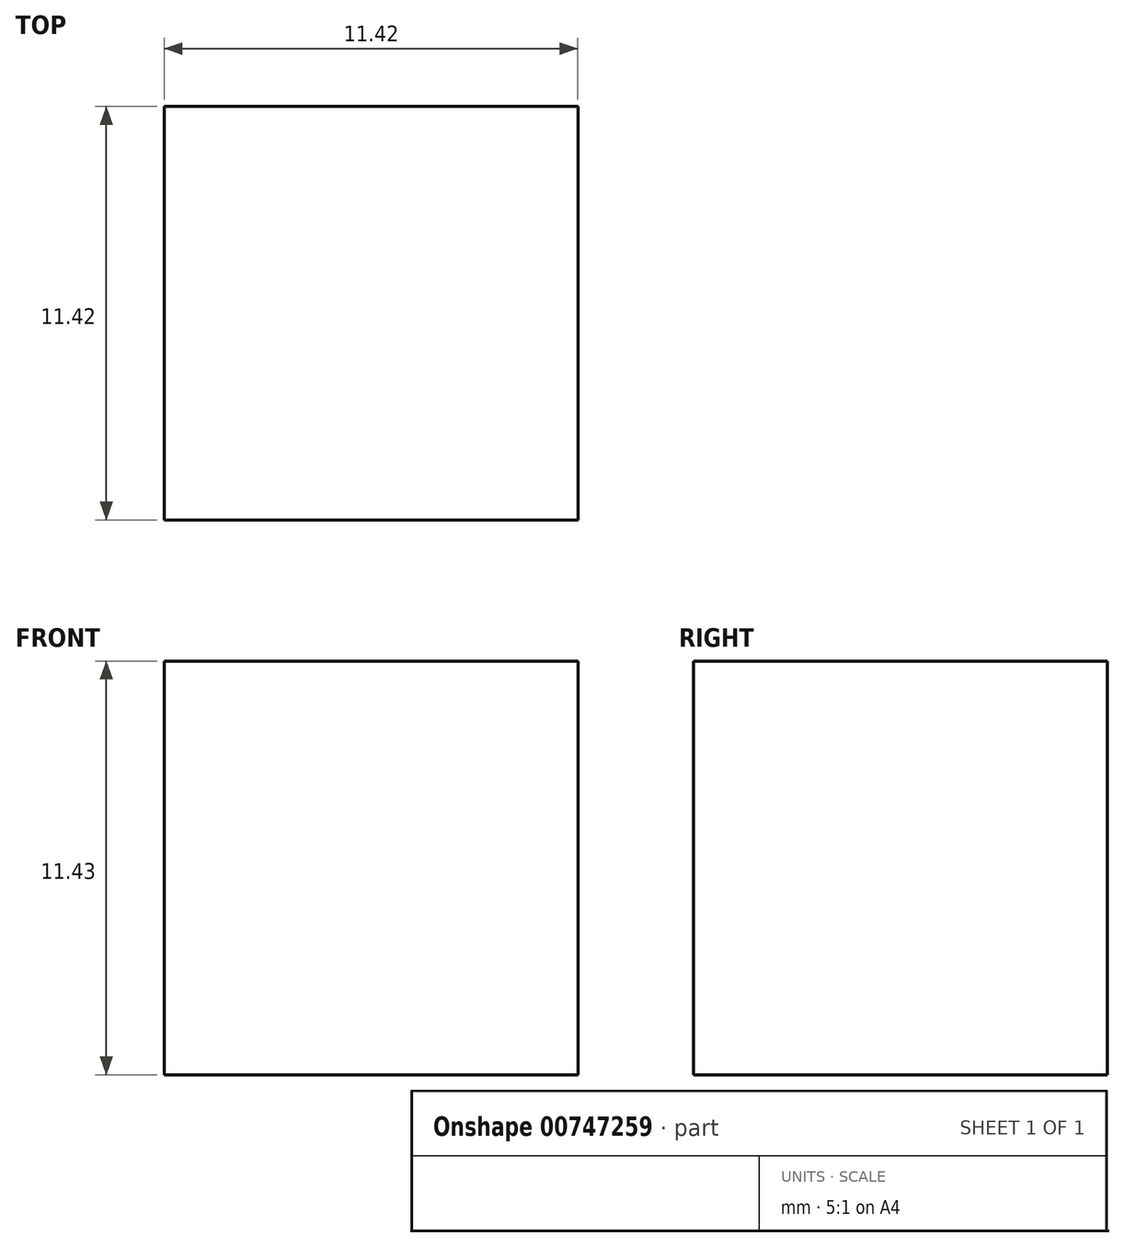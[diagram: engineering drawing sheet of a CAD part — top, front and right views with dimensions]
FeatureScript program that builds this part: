
annotation { "Feature Type Name" : "Feature", "Feature Type Description" : "" }
export const myFeature = defineFeature(function(context is Context, id is Id, definition is map)
    precondition{}
    {
        {
            var Q0;
            Q0=qCreatedBy(makeId("Top.planeOp"),FACE);
            var sketch = newSketch(context, id + "F0", { "sketchPlane" : qUnion([Q0])});
            skLineSegment(sketch, "E0.bottom", {"start": v(-5.72, 5.72) * mm, "end": v(5.72, 5.72) * mm});
            skLineSegment(sketch, "E0.top", {"start": v(-5.72, -5.71) * mm, "end": v(5.71, -5.71) * mm});
            skLineSegment(sketch, "E0.left", {"start": v(-5.72, 5.72) * mm, "end": v(-5.72, -5.71) * mm});
            skLineSegment(sketch, "E0.right", {"start": v(5.72, 5.72) * mm, "end": v(5.71, -5.71) * mm});
            skPoint(sketch, "E0.middle", {"position": v(0, 0) * mm});
            skSolve(sketch);
        }
        {
            var Q0;
            Q0 = qSketchRegion(id + "F0", true);
            extrude(context, id + "F1", {"entities" : qUnion([Q0]), "depth" : 11.43 * mm, "offsetDistance" : 25.4 * mm});
        }
    });
